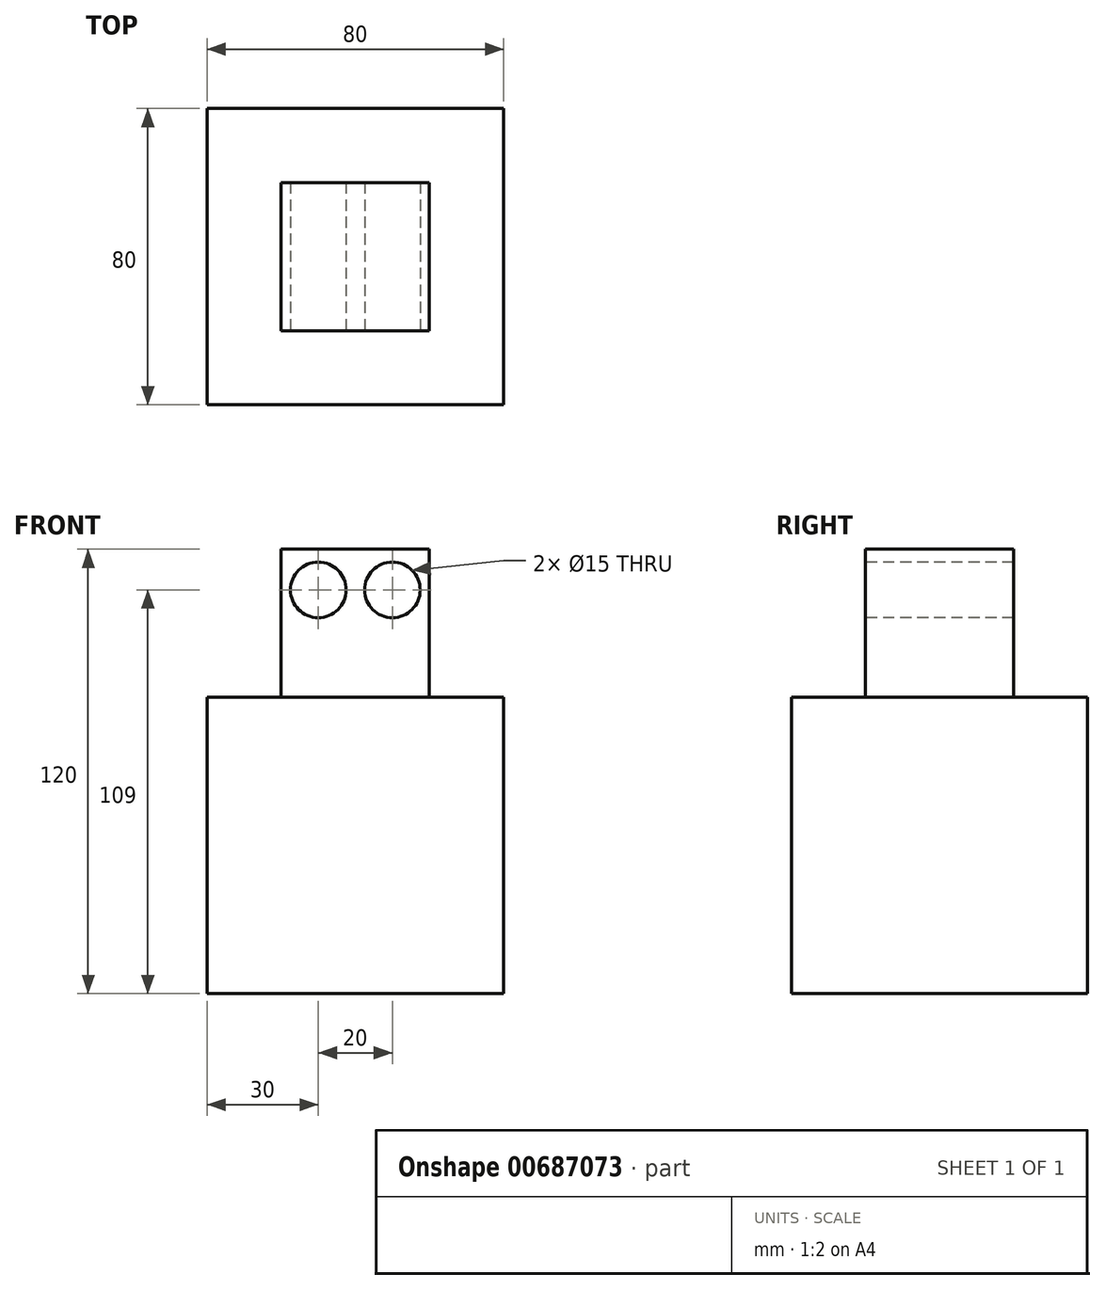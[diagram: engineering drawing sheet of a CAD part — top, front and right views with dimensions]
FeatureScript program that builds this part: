
annotation { "Feature Type Name" : "Feature", "Feature Type Description" : "" }
export const myFeature = defineFeature(function(context is Context, id is Id, definition is map)
    precondition{}
    {
        {
            var Q0;
            Q0=qCreatedBy(makeId("Top.planeOp"),FACE);
            var sketch = newSketch(context, id + "F0", { "sketchPlane" : qUnion([Q0])});
            skLineSegment(sketch, "E0.bottom", {"start": v(-40, 40) * mm, "end": v(40, 40) * mm});
            skLineSegment(sketch, "E0.top", {"start": v(-40, -40) * mm, "end": v(40, -40) * mm});
            skLineSegment(sketch, "E0.left", {"start": v(-40, 40) * mm, "end": v(-40, -40) * mm});
            skLineSegment(sketch, "E0.right", {"start": v(40, 40) * mm, "end": v(40, -40) * mm});
            skPoint(sketch, "E0.middle", {"position": v(0, 0) * mm});
            skSolve(sketch);
        }
        {
            var Q0;
            Q0 = qSketchRegion(id + "F0", true);
            extrude(context, id + "F1", {"entities" : qUnion([Q0]), "depth" : 80 * mm, "offsetDistance" : 25 * mm});
        }
        {
            var Q0;
            Q0=makeQuery(id+"F1.opExtrude","CAP_FACE",FACE,{"disambiguationData":[OSD([sQuery(id+"F0.wireOp",EDGE,"E0.bottom"),sQuery(id+"F0.wireOp",EDGE,"E0.top"),sQuery(id+"F0.wireOp",EDGE,"E0.left"),sQuery(id+"F0.wireOp",EDGE,"E0.right")])],"isStart":false});
            var sketch = newSketch(context, id + "F2", { "sketchPlane" : qUnion([Q0])});
            skLineSegment(sketch, "E1.bottom", {"start": v(-20, 20) * mm, "end": v(20, 20) * mm});
            skLineSegment(sketch, "E1.top", {"start": v(-20, -20) * mm, "end": v(20, -20) * mm});
            skLineSegment(sketch, "E1.left", {"start": v(-20, 20) * mm, "end": v(-20, -20) * mm});
            skLineSegment(sketch, "E1.right", {"start": v(20, 20) * mm, "end": v(20, -20) * mm});
            skPoint(sketch, "E1.middle", {"position": v(0, 0) * mm});
            skSolve(sketch);
        }
        {
            var Q0;
            Q0 = qSketchRegion(id + "F2", true);
            extrude(context, id + "F3", {"entities" : qUnion([Q0]), "operationType" : NewBodyOperationType.ADD, "depth" : 40 * mm, "offsetDistance" : 25 * mm});
        }
        {
            var Q0;
            Q0=makeQuery(id+"F3.opExtrude","SWEPT_FACE",FACE,{"disambiguationData":[OSD([sQuery(id+"F2.wireOp",EDGE,"E1.top")])]});
            var sketch = newSketch(context, id + "F4", { "sketchPlane" : qUnion([Q0])});
            skCircle(sketch, "E2", {"center": v(-10, 109) * mm, "radius": 7.5 * mm});
            skSolve(sketch);
        }
        {
            var Q0;
            Q0 = qSketchRegion(id + "F4", true);
            extrude(context, id + "F5", {"entities" : qUnion([Q0]), "operationType" : NewBodyOperationType.REMOVE, "oppositeDirection" : true, "depth" : 40 * mm, "offsetDistance" : 25 * mm});
        }
        {
            var Q0;
            Q0=makeQuery(id+"F3.opExtrude","SWEPT_FACE",FACE,{"disambiguationData":[OSD([sQuery(id+"F2.wireOp",EDGE,"E1.top")])]});
            var sketch = newSketch(context, id + "F6", { "sketchPlane" : qUnion([Q0])});
            skCircle(sketch, "E3", {"center": v(10, 109) * mm, "radius": 7.5 * mm});
            skSolve(sketch);
        }
        {
            var Q0;
            Q0 = qSketchRegion(id + "F6", true);
            extrude(context, id + "F7", {"entities" : qUnion([Q0]), "operationType" : NewBodyOperationType.REMOVE, "oppositeDirection" : true, "depth" : 40 * mm, "offsetDistance" : 25 * mm});
        }
    });
